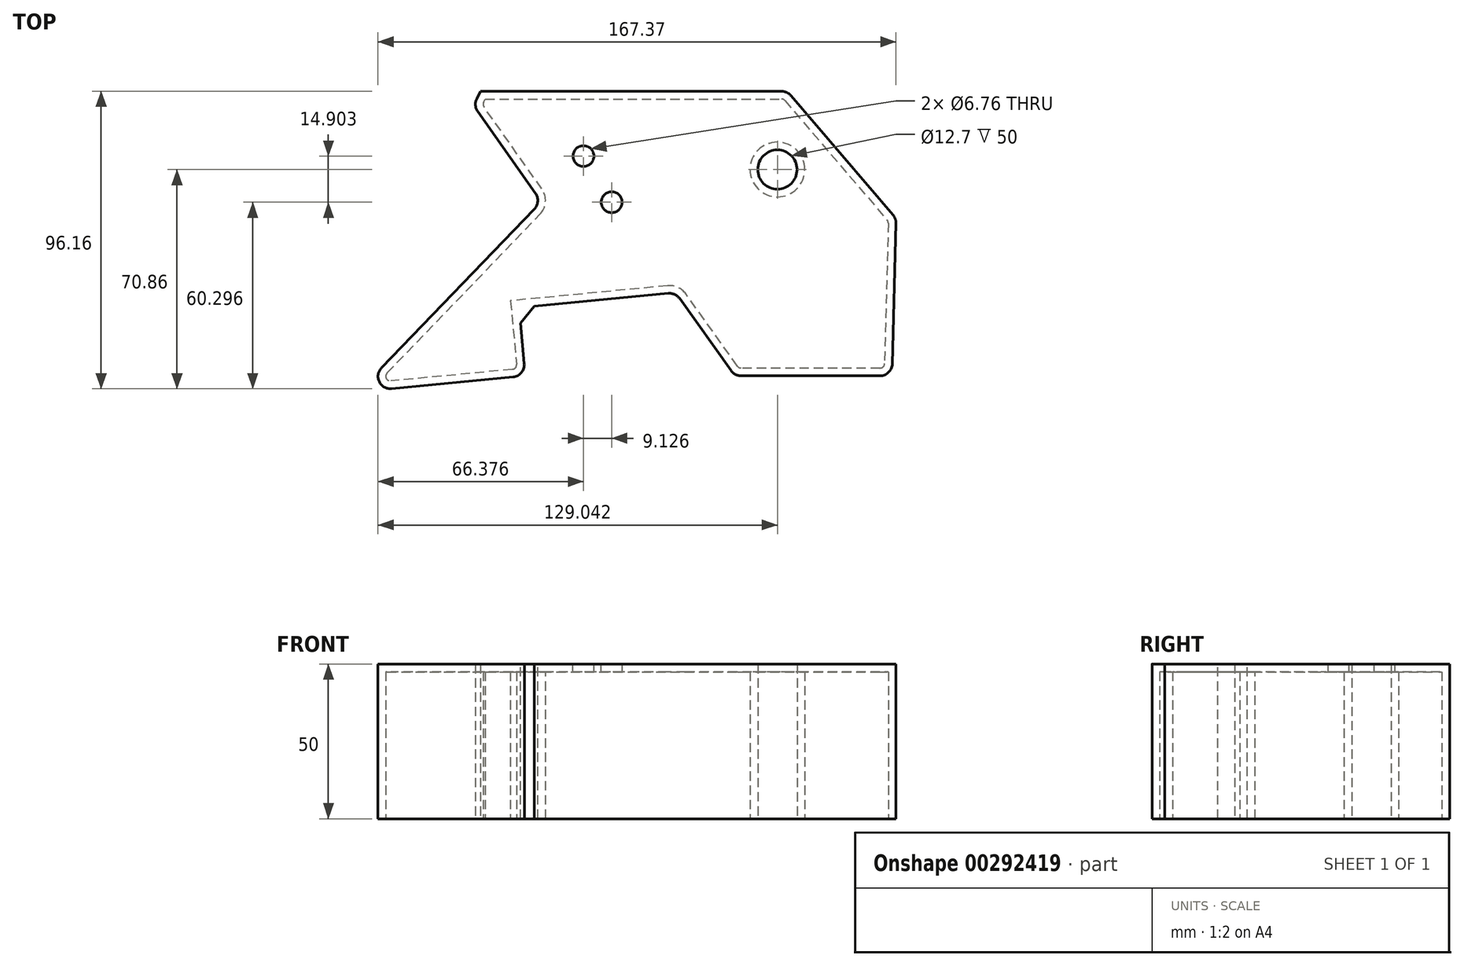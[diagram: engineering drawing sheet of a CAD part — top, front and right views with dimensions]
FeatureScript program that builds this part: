
annotation { "Feature Type Name" : "Feature", "Feature Type Description" : "" }
export const myFeature = defineFeature(function(context is Context, id is Id, definition is map)
    precondition{}
    {
        {
            var Q0;
            Q0=qCreatedBy(makeId("Top.planeOp"),FACE);
            var sketch = newSketch(context, id + "F0", { "sketchPlane" : qUnion([Q0])});
            skLineSegment(sketch, "E0", {"start": v(-49.35, 49.02) * mm, "end": v(49.7, 49.02) * mm});
            skLineSegment(sketch, "E1", {"start": v(49.7, 49.02) * mm, "end": v(84.95, 7.83) * mm});
            skLineSegment(sketch, "E2", {"start": v(84.95, 7.83) * mm, "end": v(83.62, -42.97) * mm});
            skLineSegment(sketch, "E3", {"start": v(83.62, -42.97) * mm, "end": v(32.82, -42.97) * mm});
            skLineSegment(sketch, "E4", {"start": v(32.82, -42.97) * mm, "end": v(13.63, -16.1) * mm});
            skLineSegment(sketch, "E5", {"start": v(13.63, -16.1) * mm, "end": v(-36.94, -20.96) * mm});
            skLineSegment(sketch, "E6", {"start": v(-36.94, -20.96) * mm, "end": v(-34.82, -42.97) * mm});
            skLineSegment(sketch, "E7", {"start": v(-34.82, -42.97) * mm, "end": v(-88.84, -48.16) * mm});
            skLineSegment(sketch, "E8", {"start": v(-88.84, -48.16) * mm, "end": v(-29.67, 13.33) * mm});
            skLineSegment(sketch, "E9", {"start": v(-29.67, 13.33) * mm, "end": v(-51.64, 44.45) * mm});
            skLineSegment(sketch, "E10", {"start": v(-51.64, 44.45) * mm, "end": v(-49.35, 49.02) * mm});
            skCircle(sketch, "E11", {"center": v(46.58, 23.72) * mm, "radius": 6.35 * mm});
            skSolve(sketch);
        }
        {
            var Q0;
            Q0=makeQuery(id+"F0.imprint","IMPRINT",FACE,{"disambiguationData":[TD([[makeQuery(id+"F0.imprint","IMPRINT",EDGE,{"derivedFrom":sQuery(id+"F0.wireOp",EDGE,"E0")}),-1.0]])]});
            extrude(context, id + "F1", {"entities" : qUnion([Q0]), "depth" : 50 * mm});
        }
        {
            var Q0;
            Q0=makeQuery(id+"F1.opExtrude","SWEPT_EDGE",EDGE,{"disambiguationData":[OSD([sQuery(id+"F0.wireOp",EDGE,"E1"),sQuery(id+"F0.wireOp",EDGE,"E2")])]});
            var Q1;
            Q1=makeQuery(id+"F1.opExtrude","SWEPT_EDGE",EDGE,{"disambiguationData":[OSD([sQuery(id+"F0.wireOp",EDGE,"E2"),sQuery(id+"F0.wireOp",EDGE,"E3")])]});
            var Q2;
            Q2=makeQuery(id+"F1.opExtrude","SWEPT_EDGE",EDGE,{"disambiguationData":[OSD([sQuery(id+"F0.wireOp",EDGE,"E6"),sQuery(id+"F0.wireOp",EDGE,"E7")])]});
            var Q3;
            Q3=makeQuery(id+"F1.opExtrude","SWEPT_EDGE",EDGE,{"disambiguationData":[OSD([sQuery(id+"F0.wireOp",EDGE,"E3"),sQuery(id+"F0.wireOp",EDGE,"E4")])]});
            var Q4;
            Q4=makeQuery(id+"F1.opExtrude","SWEPT_EDGE",EDGE,{"disambiguationData":[OSD([sQuery(id+"F0.wireOp",EDGE,"E7"),sQuery(id+"F0.wireOp",EDGE,"E8")])]});
            var Q5;
            Q5=makeQuery(id+"F1.opExtrude","SWEPT_EDGE",EDGE,{"disambiguationData":[OSD([sQuery(id+"F0.wireOp",EDGE,"E0"),sQuery(id+"F0.wireOp",EDGE,"E1")])]});
            var Q6;
            Q6=makeQuery(id+"F1.opExtrude","SWEPT_EDGE",EDGE,{"disambiguationData":[OSD([sQuery(id+"F0.wireOp",EDGE,"E8"),sQuery(id+"F0.wireOp",EDGE,"E9")])]});
            var Q7;
            Q7=makeQuery(id+"F1.opExtrude","SWEPT_EDGE",EDGE,{"disambiguationData":[OSD([sQuery(id+"F0.wireOp",EDGE,"E9"),sQuery(id+"F0.wireOp",EDGE,"E10")])]});
            var Q8;
            Q8=makeQuery(id+"F1.opExtrude","SWEPT_EDGE",EDGE,{"disambiguationData":[OSD([sQuery(id+"F0.wireOp",EDGE,"E4"),sQuery(id+"F0.wireOp",EDGE,"E5")])]});
            fillet(context, id + "F2", {"entities" : qUnion([Q0, Q1, Q2, Q3, Q4, Q5, Q6, Q7, Q8]), "radius" : 4 * mm, "tangentPropagation" : true, "allowEdgeOverflow" : false});
        }
        {
            var Q0;
            Q0=makeQuery(id+"F1.opExtrude","CAP_FACE",FACE,{"disambiguationData":[OSD([sQuery(id+"F0.wireOp",EDGE,"E0"),sQuery(id+"F0.wireOp",EDGE,"E1"),sQuery(id+"F0.wireOp",EDGE,"E2"),sQuery(id+"F0.wireOp",EDGE,"E3"),sQuery(id+"F0.wireOp",EDGE,"E4"),sQuery(id+"F0.wireOp",EDGE,"E5"),sQuery(id+"F0.wireOp",EDGE,"E6"),sQuery(id+"F0.wireOp",EDGE,"E7"),sQuery(id+"F0.wireOp",EDGE,"E8"),sQuery(id+"F0.wireOp",EDGE,"E9"),sQuery(id+"F0.wireOp",EDGE,"E10"),sQuery(id+"F0.wireOp",EDGE,"E11")])],"isStart":true});
            shell(context, id + "F3", {"entities" : qUnion([Q0]), "thickness" : 2.5 * mm});
        }
        {
            var Q0;
            Q0=makeQuery(id+"F1.opExtrude","CAP_FACE",FACE,{"disambiguationData":[OSD([sQuery(id+"F0.wireOp",EDGE,"E0"),sQuery(id+"F0.wireOp",EDGE,"E1"),sQuery(id+"F0.wireOp",EDGE,"E2"),sQuery(id+"F0.wireOp",EDGE,"E3"),sQuery(id+"F0.wireOp",EDGE,"E4"),sQuery(id+"F0.wireOp",EDGE,"E5"),sQuery(id+"F0.wireOp",EDGE,"E6"),sQuery(id+"F0.wireOp",EDGE,"E7"),sQuery(id+"F0.wireOp",EDGE,"E8"),sQuery(id+"F0.wireOp",EDGE,"E9"),sQuery(id+"F0.wireOp",EDGE,"E10"),sQuery(id+"F0.wireOp",EDGE,"E11")])],"isStart":false});
            var sketch = newSketch(context, id + "F4", { "sketchPlane" : qUnion([Q0])});
            skCircle(sketch, "E12", {"center": v(-6.96, 13.16) * mm, "radius": 2.5 * mm});
            skCircle(sketch, "E13", {"center": v(-16.08, 28.06) * mm, "radius": 2.5 * mm});
            skSolve(sketch);
        }
        {
            var Q0;
            Q0=sQuery(id+"F4.wireOp",VERTEX,"E12.center");
            var Q1;
            Q1=sQuery(id+"F4.wireOp",VERTEX,"E13.center");
            var Q2;
            Q2=makeQuery(id+"F1.opExtrude","SWEPT_BODY",BODY,{"disambiguationData":[OSD([sQuery(id+"F0.wireOp",EDGE,"E0"),sQuery(id+"F0.wireOp",EDGE,"E1"),sQuery(id+"F0.wireOp",EDGE,"E2"),sQuery(id+"F0.wireOp",EDGE,"E3"),sQuery(id+"F0.wireOp",EDGE,"E4"),sQuery(id+"F0.wireOp",EDGE,"E5"),sQuery(id+"F0.wireOp",EDGE,"E6"),sQuery(id+"F0.wireOp",EDGE,"E7"),sQuery(id+"F0.wireOp",EDGE,"E8"),sQuery(id+"F0.wireOp",EDGE,"E9"),sQuery(id+"F0.wireOp",EDGE,"E10"),sQuery(id+"F0.wireOp",EDGE,"E11")])]});
            hole(context, id + "F5", {"style" : HoleStyle.SIMPLE, "endStyle" : HoleEndStyle.THROUGH, "holeDiameter" : 6.76 * mm, "tappedDepth" : 12 * mm, "tapClearance" : 3, "locations" : qUnion([Q0, Q1]), "scope" : qUnion([Q2])});
        }
        {
            var Q0;
            Q0=makeQuery(id+"F1.opExtrude","SWEPT_EDGE",EDGE,{"disambiguationData":[OSD([sQuery(id+"F0.wireOp",EDGE,"E5"),sQuery(id+"F0.wireOp",EDGE,"E6")])]});
            chamfer(context, id + "F6", {"entities" : qUnion([Q0]), "width" : 5 * mm, "tangentPropagation" : true});
        }
    });
